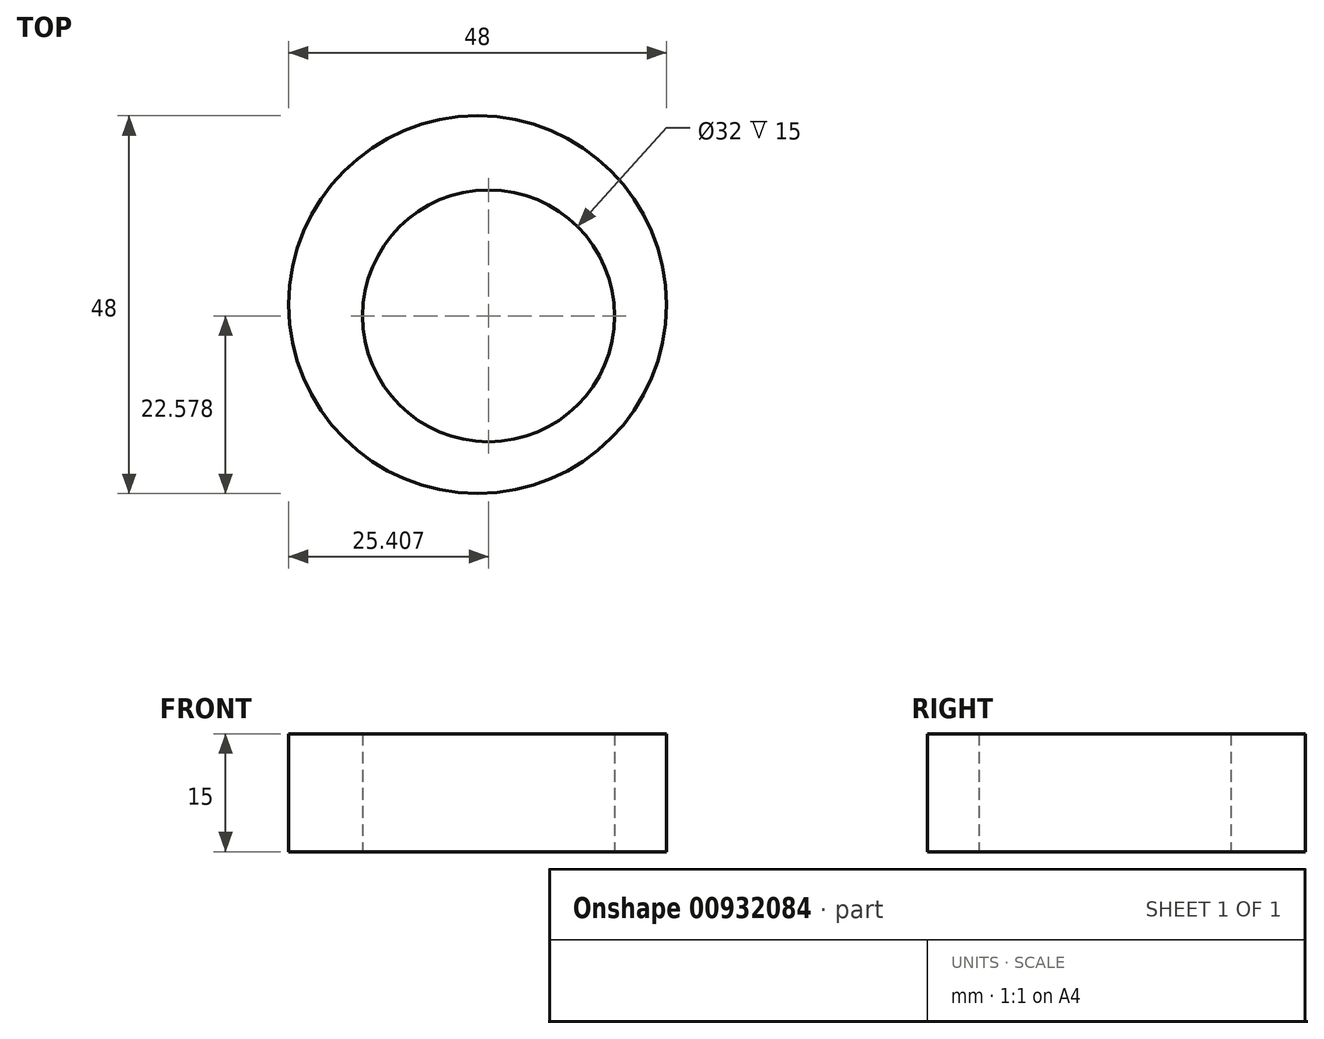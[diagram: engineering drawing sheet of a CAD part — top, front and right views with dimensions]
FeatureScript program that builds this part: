
annotation { "Feature Type Name" : "Feature", "Feature Type Description" : "" }
export const myFeature = defineFeature(function(context is Context, id is Id, definition is map)
    precondition{}
    {
        {
            var Q0;
            Q0=qCreatedBy(makeId("Top.planeOp"),FACE);
            var sketch = newSketch(context, id + "F0", { "sketchPlane" : qUnion([Q0])});
            skCircle(sketch, "E0", {"center": v(0, 0) * mm, "radius": 24 * mm});
            skCircle(sketch, "E1", {"center": v(1.4, -1.42) * mm, "radius": 16 * mm});
            skSolve(sketch);
        }
        {
            var Q0;
            Q0=makeQuery(id+"F0.imprint","IMPRINT",FACE,{"disambiguationData":[TD([[makeQuery(id+"F0.imprint","IMPRINT",EDGE,{"derivedFrom":sQuery(id+"F0.wireOp",EDGE,"E0")}),1.0]])]});
            extrude(context, id + "F1", {"entities" : qUnion([Q0]), "depth" : 15 * mm, "offsetDistance" : 25 * mm});
        }
    });
